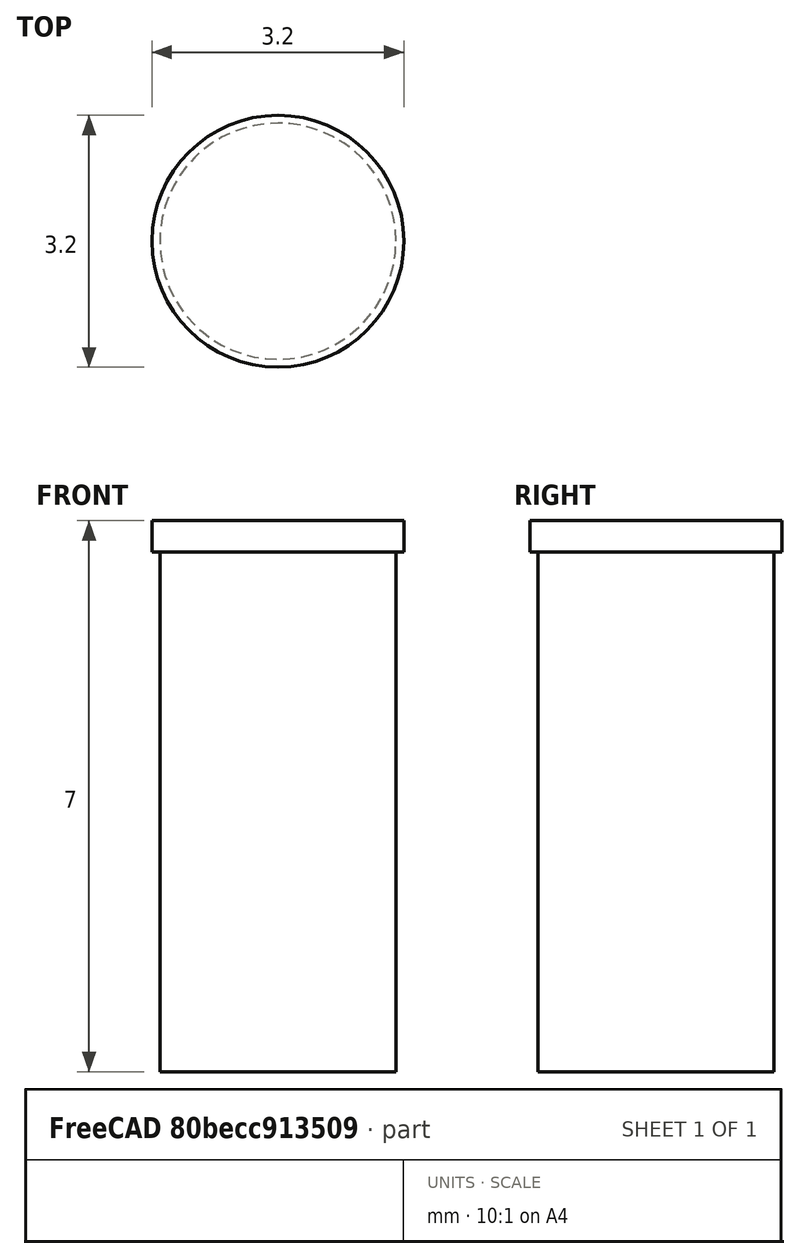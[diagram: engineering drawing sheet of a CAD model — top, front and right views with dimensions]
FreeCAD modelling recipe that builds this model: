
FCSTD DOCUMENT  (FreeCAD 0.18R15969 (Git))
Label: lightpipe
License: All rights reserved
LicenseURL: http://en.wikipedia.org/wiki/All_rights_reserved
objects: Sketcher::SketchObject×1, PartDesign::Revolution×1, PartDesign::Body×1
note: 4 computed .brp shape members not serialized (recipe doc carries the construction recipe); baked Part::Feature solids carry a one-line shape summary decoded from their .brp

FEATURE [Sketcher::SketchObject] Sketch
  MapMode = 5
  Placement = pos=(0,0,0) rot=(0.57735,0.57735,0.57735;2.0944rad)
  Support = -> [YZ_Plane]
  sketch-geometry (6):
    g0: LineSegment StartX=0 StartY=0 StartZ=0 EndX=-1.6 EndY=0 EndZ=0
    g1: LineSegment StartX=-1.6 StartY=0 StartZ=0 EndX=-1.6 EndY=-0.4 EndZ=0
    g2: LineSegment StartX=-1.6 StartY=-0.4 StartZ=0 EndX=-1.5 EndY=-0.4 EndZ=0
    g3: LineSegment StartX=-1.5 StartY=-0.4 StartZ=0 EndX=-1.5 EndY=-7 EndZ=0
    g4: LineSegment StartX=-1.5 StartY=-7 StartZ=0 EndX=0 EndY=-7 EndZ=0
    g5: LineSegment StartX=0 StartY=-7 StartZ=0 EndX=0 EndY=0 EndZ=0
  constraints (17):
    c: Coincident(g0,g-1)
    c: Horizontal(g0)
    c: Coincident(g1,g0)
    c: Coincident(g2,g1)
    c: Coincident(g3,g2)
    c: Vertical(g3)
    c: Coincident(g4,g3)
    c: Coincident(g5,g4)
    c: Coincident(g5,g-1)
    c: Vertical(g5)
    c: Horizontal(g4)
    c: Horizontal(g2)
    c: Vertical(g1)
    c: DistanceY(g1,g1) = 0.4
    c: DistanceX(g4,g4) = 1.5
    c: DistanceX(g0,g0) = 1.6
    c: DistanceY(g5,g5) = 7
FEATURE [PartDesign::Revolution] Revolution
  Angle = 360
  Axis = (0,0,1)
  Base = (0,0,0)
  Placement = pos=(0,0,0) rot=(0.57735,0.57735,0.57735;2.0944rad)
  Profile = -> Sketch
  ReferenceAxis = -> Sketch [V_Axis]
FEATURE [PartDesign::Body] Body
  Group = -> [Sketch,Revolution]
  Origin = -> Origin
  Tip = -> Revolution
